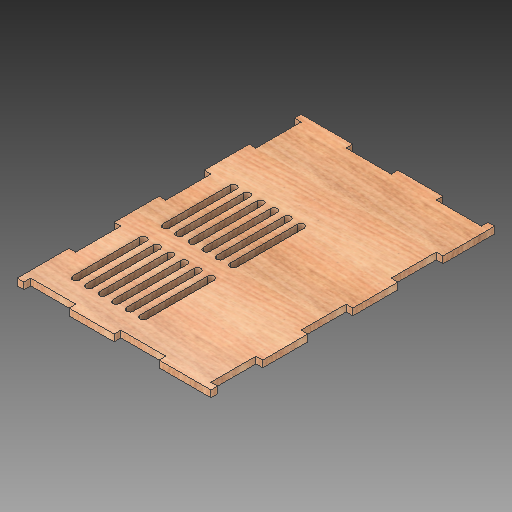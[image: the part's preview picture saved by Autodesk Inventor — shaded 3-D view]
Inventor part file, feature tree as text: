
AUTODESK INVENTOR PART (.ipt)
format: ipt  version: 2018.2 (Build 222227000, 227)  size: 366,592 bytes
history: native  units: mm
features: extrude x2, pattern_linear x2, sketch x2
ambient origin geometry x8: Origin, YZ Plane, XZ Plane, XY Plane, X Axis, Y Axis, Z Axis, Center Point
bodies: Body1 (feature_tree)
feature tree (6):
  extrude  "Extrusion3"  Depth=80.0mm
  extrude  "Extrusion4"  Depth=20.0mm
  pattern_linear  "Rectangular Pattern2"  Count1=2 Spacing1=10.0mm
  pattern_linear  "Rectangular Pattern3"  Spacing1=3.0mm  [1 undecoded]
  sketch  "Sketch1"  dims[d0=120.0mm d1=80.0mm]
  sketch  "Sketch2"  dims[d2=3.0mm d3=20.0mm d11=20.0mm d13=40.0mm d14=10.0mm d16=10.0mm d18=3.0mm d19=20.0mm d20=20.0mm d22=40.0mm d23=10.0mm d25=10.0mm d27=3.0mm d28=20.0mm d29=30.0mm d31=40.0mm d32=10.0mm d34=10.0mm d36=3.0mm d37=20.0mm d38=30.0mm d40=40.0mm d41=10.0mm d43=10.0mm d45=3.0mm d46=0.0mm d47=3.0mm d48=3.0mm d49=3.0mm d50=30.0mm d51=3.0mm d52=10.0mm d53=10.0mm d54=10.0mm d55=0.0mm d56=20.0mm d58=40.0mm d59=60.0mm d61=6.0mm]
note: 1 required parameter value undecoded (feature->parameter linkage not recoverable at this tier; creation-order binding heuristic only, values carry confidence <= 0.55)
